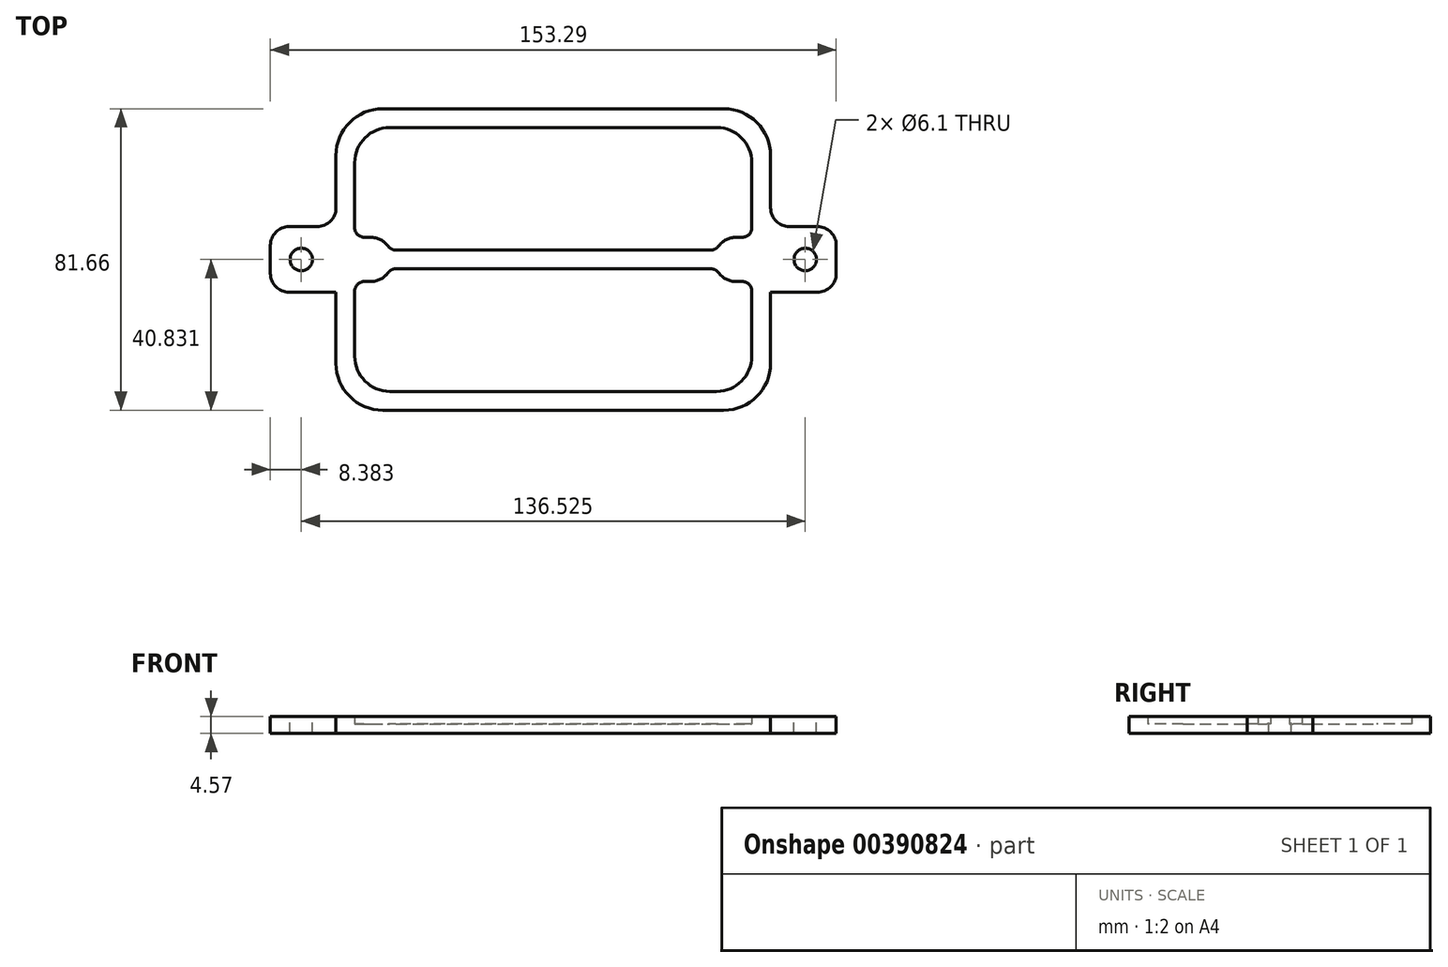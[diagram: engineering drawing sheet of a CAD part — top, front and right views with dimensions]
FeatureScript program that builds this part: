
annotation { "Feature Type Name" : "Feature", "Feature Type Description" : "" }
export const myFeature = defineFeature(function(context is Context, id is Id, definition is map)
    precondition{}
    {
        {
            var Q0;
            Q0=qCreatedBy(makeId("Top.planeOp"),FACE);
            var sketch = newSketch(context, id + "F0", { "sketchPlane" : qUnion([Q0])});
            skLineSegment(sketch, "E0.bottom", {"start": v(0, 0) * mm, "end": v(-117.73, 0) * mm});
            skLineSegment(sketch, "E0.top", {"start": v(0, 81.66) * mm, "end": v(-117.73, 81.66) * mm});
            skLineSegment(sketch, "E0.left", {"start": v(0, 0) * mm, "end": v(0, 81.66) * mm});
            skLineSegment(sketch, "E0.right", {"start": v(-117.73, 0) * mm, "end": v(-117.73, 81.66) * mm});
            skSolve(sketch);
        }
        {
            var Q0;
            Q0 = qSketchRegion(id + "F0", true);
            extrude(context, id + "F1", {"entities" : qUnion([Q0]), "depth" : 2.54 * mm});
        }
        {
            var Q0;
            Q0=makeQuery(id+"F1.opExtrude","CAP_FACE",FACE,{"disambiguationData":[OSD([sQuery(id+"F0.wireOp",EDGE,"E0.bottom"),sQuery(id+"F0.wireOp",EDGE,"E0.top"),sQuery(id+"F0.wireOp",EDGE,"E0.left"),sQuery(id+"F0.wireOp",EDGE,"E0.right")])],"isStart":false});
            var sketch = newSketch(context, id + "F2", { "sketchPlane" : qUnion([Q0])});
            skLineSegment(sketch, "E1.0", {"start": v(-14.6, 5.08) * mm, "end": v(-103.12, 5.08) * mm});
            skLineSegment(sketch, "E1.1", {"start": v(-5.08, 14.6) * mm, "end": v(-5.08, 32.3) * mm});
            skLineSegment(sketch, "E1.2", {"start": v(-14.6, 76.58) * mm, "end": v(-103.12, 76.58) * mm});
            skLineSegment(sketch, "E1.3", {"start": v(-112.65, 14.6) * mm, "end": v(-112.65, 32.3) * mm});
            skArc(sketch, "E2", {"start": v(-108.4, 34.83) * mm, "mid": v(-105.7, 35.47) * mm, "end": v(-103.57, 37.26) * mm});
            skLineSegment(sketch, "E3", {"start": v(-110.1, 34.83) * mm, "end": v(-108.4, 34.83) * mm});
            skLineSegment(sketch, "E4", {"start": v(-110.1, 46.83) * mm, "end": v(-108.4, 46.83) * mm});
            skLineSegment(sketch, "E5.trimOffspring", {"start": v(-112.65, 49.37) * mm, "end": v(-112.65, 67.06) * mm});
            skLineSegment(sketch, "E6", {"start": v(-58.86, 0) * mm, "end": v(-58.86, 38.3) * mm, "construction": true});
            skLineSegment(sketch, "E7.bottom", {"start": v(-101.53, 43.37) * mm, "end": v(-58.86, 43.37) * mm});
            skLineSegment(sketch, "E7.top", {"start": v(-101.53, 38.3) * mm, "end": v(-58.86, 38.3) * mm});
            skArc(sketch, "E8.trimOffspring", {"start": v(-103.57, 44.4) * mm, "mid": v(-105.7, 46.19) * mm, "end": v(-108.4, 46.83) * mm});
            skLineSegment(sketch, "E9.MirrorCS", {"start": v(-7.62, 46.83) * mm, "end": v(-9.33, 46.83) * mm});
            skArc(sketch, "E10.MirrorCS", {"start": v(-14.16, 44.4) * mm, "mid": v(-12.04, 46.19) * mm, "end": v(-9.33, 46.83) * mm});
            skLineSegment(sketch, "E11.MirrorCS", {"start": v(-16.2, 43.37) * mm, "end": v(-58.86, 43.37) * mm});
            skLineSegment(sketch, "E12.MirrorCS", {"start": v(-16.2, 38.3) * mm, "end": v(-58.86, 38.3) * mm});
            skArc(sketch, "E13.MirrorCS", {"start": v(-9.33, 34.83) * mm, "mid": v(-12.04, 35.47) * mm, "end": v(-14.16, 37.26) * mm});
            skLineSegment(sketch, "E14.MirrorCS", {"start": v(-7.62, 34.83) * mm, "end": v(-9.33, 34.83) * mm});
            skLineSegment(sketch, "E15.trimOffspring", {"start": v(-58.86, 43.37) * mm, "end": v(-58.86, 81.66) * mm, "construction": true});
            skLineSegment(sketch, "E16.trimOffspring", {"start": v(-5.08, 49.37) * mm, "end": v(-5.08, 67.06) * mm});
            skPoint(sketch, "E17.visualSharp", {"position": v(-112.65, 76.58) * mm});
            skArc(sketch, "E17.filletArc", {"start": v(-103.12, 76.58) * mm, "mid": v(-109.86, 73.8) * mm, "end": v(-112.65, 67.06) * mm});
            skPoint(sketch, "E18.visualSharp", {"position": v(-5.08, 76.58) * mm});
            skArc(sketch, "E18.filletArc", {"start": v(-5.08, 67.06) * mm, "mid": v(-7.87, 73.8) * mm, "end": v(-14.6, 76.58) * mm});
            skPoint(sketch, "E19.visualSharp", {"position": v(-5.08, 5.08) * mm});
            skArc(sketch, "E19.filletArc", {"start": v(-14.6, 5.08) * mm, "mid": v(-7.87, 7.87) * mm, "end": v(-5.08, 14.6) * mm});
            skPoint(sketch, "E20.visualSharp", {"position": v(-112.65, 5.08) * mm});
            skArc(sketch, "E20.filletArc", {"start": v(-112.65, 14.6) * mm, "mid": v(-109.86, 7.87) * mm, "end": v(-103.12, 5.08) * mm});
            skPoint(sketch, "E21.visualSharp", {"position": v(-112.65, 34.83) * mm});
            skArc(sketch, "E21.filletArc", {"start": v(-110.1, 34.83) * mm, "mid": v(-111.9, 34.09) * mm, "end": v(-112.65, 32.3) * mm});
            skPoint(sketch, "E22.visualSharp", {"position": v(-112.65, 46.83) * mm});
            skArc(sketch, "E22.filletArc", {"start": v(-112.65, 49.37) * mm, "mid": v(-111.9, 47.57) * mm, "end": v(-110.1, 46.83) * mm});
            skPoint(sketch, "E23.visualSharp", {"position": v(-102.96, 43.37) * mm});
            skArc(sketch, "E23.filletArc", {"start": v(-103.57, 44.4) * mm, "mid": v(-102.67, 43.64) * mm, "end": v(-101.53, 43.37) * mm});
            skPoint(sketch, "E24.visualSharp", {"position": v(-102.96, 38.3) * mm});
            skArc(sketch, "E24.filletArc", {"start": v(-101.53, 38.3) * mm, "mid": v(-102.67, 38.02) * mm, "end": v(-103.57, 37.26) * mm});
            skPoint(sketch, "E25.visualSharp", {"position": v(-5.08, 34.83) * mm});
            skArc(sketch, "E25.filletArc", {"start": v(-5.08, 32.3) * mm, "mid": v(-5.82, 34.09) * mm, "end": v(-7.62, 34.83) * mm});
            skPoint(sketch, "E26.visualSharp", {"position": v(-5.08, 46.83) * mm});
            skArc(sketch, "E26.filletArc", {"start": v(-7.62, 46.83) * mm, "mid": v(-5.82, 47.57) * mm, "end": v(-5.08, 49.37) * mm});
            skPoint(sketch, "E27.visualSharp", {"position": v(-14.77, 43.37) * mm});
            skArc(sketch, "E27.filletArc", {"start": v(-16.2, 43.37) * mm, "mid": v(-15.06, 43.64) * mm, "end": v(-14.16, 44.4) * mm});
            skPoint(sketch, "E28.visualSharp", {"position": v(-14.77, 38.3) * mm});
            skArc(sketch, "E28.filletArc", {"start": v(-14.16, 37.26) * mm, "mid": v(-15.06, 38.02) * mm, "end": v(-16.2, 38.3) * mm});
            skLineSegment(sketch, "E29.0", {"start": v(0, 81.66) * mm, "end": v(-117.73, 81.66) * mm});
            skLineSegment(sketch, "E30.0", {"start": v(-117.73, 0) * mm, "end": v(-117.73, 81.66) * mm});
            skLineSegment(sketch, "E31.0", {"start": v(0, 0) * mm, "end": v(-117.73, 0) * mm});
            skLineSegment(sketch, "E32.0", {"start": v(0, 0) * mm, "end": v(0, 81.66) * mm});
            skSolve(sketch);
        }
        {
            var Q0;
            Q0 = qSketchRegion(id + "F2", true);
            extrude(context, id + "F3", {"entities" : qUnion([Q0]), "operationType" : NewBodyOperationType.ADD, "depth" : 2.03 * mm});
        }
        {
            var Q0;
            Q0=makeQuery(id+"F3.boolean.opBoolean","MERGE",EDGE,{"derivedFrom":[makeQuery(id+"F1.opExtrude","SWEPT_EDGE",EDGE,{"disambiguationData":[OSD([sQuery(id+"F0.wireOp",EDGE,"E0.bottom"),sQuery(id+"F0.wireOp",EDGE,"E0.right")])]}),makeQuery(id+"F3.opExtrude","SWEPT_EDGE",EDGE,{"disambiguationData":[OSD([sQuery(id+"F2.wireOp",EDGE,"E30.0"),sQuery(id+"F2.wireOp",EDGE,"E31.0")])]})]});
            var Q1;
            Q1=makeQuery(id+"F3.boolean.opBoolean","MERGE",EDGE,{"derivedFrom":[makeQuery(id+"F1.opExtrude","SWEPT_EDGE",EDGE,{"disambiguationData":[OSD([sQuery(id+"F0.wireOp",EDGE,"E0.top"),sQuery(id+"F0.wireOp",EDGE,"E0.right")])]}),makeQuery(id+"F3.opExtrude","SWEPT_EDGE",EDGE,{"disambiguationData":[OSD([sQuery(id+"F2.wireOp",EDGE,"E29.0"),sQuery(id+"F2.wireOp",EDGE,"E30.0")])]})]});
            var Q2;
            Q2=makeQuery(id+"F3.boolean.opBoolean","MERGE",EDGE,{"derivedFrom":[makeQuery(id+"F1.opExtrude","SWEPT_EDGE",EDGE,{"disambiguationData":[OSD([sQuery(id+"F0.wireOp",EDGE,"E0.top"),sQuery(id+"F0.wireOp",EDGE,"E0.left")])]}),makeQuery(id+"F3.opExtrude","SWEPT_EDGE",EDGE,{"disambiguationData":[OSD([sQuery(id+"F2.wireOp",EDGE,"E29.0"),sQuery(id+"F2.wireOp",EDGE,"E32.0")])]})]});
            var Q3;
            Q3=makeQuery(id+"F3.boolean.opBoolean","MERGE",EDGE,{"derivedFrom":[makeQuery(id+"F1.opExtrude","SWEPT_EDGE",EDGE,{"disambiguationData":[OSD([sQuery(id+"F0.wireOp",EDGE,"E0.bottom"),sQuery(id+"F0.wireOp",EDGE,"E0.left")])]}),makeQuery(id+"F3.opExtrude","SWEPT_EDGE",EDGE,{"disambiguationData":[OSD([sQuery(id+"F2.wireOp",EDGE,"E31.0"),sQuery(id+"F2.wireOp",EDGE,"E32.0")])]})]});
            fillet(context, id + "F4", {"entities" : qUnion([Q0, Q1, Q2, Q3]), "radius" : 12.7 * mm, "tangentPropagation" : true, "allowEdgeOverflow" : false});
        }
        {
            var Q0;
            Q0=makeQuery(id+"F3.opExtrude","CAP_FACE",FACE,{"disambiguationData":[OSD([sQuery(id+"F2.wireOp",EDGE,"E1.0"),sQuery(id+"F2.wireOp",EDGE,"E1.1"),sQuery(id+"F2.wireOp",EDGE,"E1.2"),sQuery(id+"F2.wireOp",EDGE,"E1.3"),sQuery(id+"F2.wireOp",EDGE,"E2"),sQuery(id+"F2.wireOp",EDGE,"E3"),sQuery(id+"F2.wireOp",EDGE,"E4"),sQuery(id+"F2.wireOp",EDGE,"E5.trimOffspring"),sQuery(id+"F2.wireOp",EDGE,"E7.bottom"),sQuery(id+"F2.wireOp",EDGE,"E7.top"),sQuery(id+"F2.wireOp",EDGE,"E8.trimOffspring"),sQuery(id+"F2.wireOp",EDGE,"E9.MirrorCS"),sQuery(id+"F2.wireOp",EDGE,"E10.MirrorCS"),sQuery(id+"F2.wireOp",EDGE,"E11.MirrorCS"),sQuery(id+"F2.wireOp",EDGE,"E12.MirrorCS"),sQuery(id+"F2.wireOp",EDGE,"E13.MirrorCS"),sQuery(id+"F2.wireOp",EDGE,"E14.MirrorCS"),sQuery(id+"F2.wireOp",EDGE,"E16.trimOffspring"),sQuery(id+"F2.wireOp",EDGE,"E17.filletArc"),sQuery(id+"F2.wireOp",EDGE,"E18.filletArc"),sQuery(id+"F2.wireOp",EDGE,"E19.filletArc"),sQuery(id+"F2.wireOp",EDGE,"E20.filletArc"),sQuery(id+"F2.wireOp",EDGE,"E21.filletArc"),sQuery(id+"F2.wireOp",EDGE,"E22.filletArc"),sQuery(id+"F2.wireOp",EDGE,"E23.filletArc"),sQuery(id+"F2.wireOp",EDGE,"E24.filletArc"),sQuery(id+"F2.wireOp",EDGE,"E25.filletArc"),sQuery(id+"F2.wireOp",EDGE,"E26.filletArc"),sQuery(id+"F2.wireOp",EDGE,"E27.filletArc"),sQuery(id+"F2.wireOp",EDGE,"E28.filletArc"),sQuery(id+"F2.wireOp",EDGE,"E29.0"),sQuery(id+"F2.wireOp",EDGE,"E30.0"),sQuery(id+"F2.wireOp",EDGE,"E31.0"),sQuery(id+"F2.wireOp",EDGE,"E32.0")])],"isStart":false});
            var sketch = newSketch(context, id + "F5", { "sketchPlane" : qUnion([Q0])});
            skLineSegment(sketch, "E33.bottom", {"start": v(0, 31.94) * mm, "end": v(17.78, 31.94) * mm});
            skLineSegment(sketch, "E33.top", {"start": v(0, 49.72) * mm, "end": v(17.78, 49.72) * mm});
            skLineSegment(sketch, "E33.left", {"start": v(0, 31.94) * mm, "end": v(0, 49.72) * mm});
            skLineSegment(sketch, "E33.right", {"start": v(17.78, 31.94) * mm, "end": v(17.78, 49.72) * mm});
            skLineSegment(sketch, "E34", {"start": v(-117.73, 40.83) * mm, "end": v(0, 40.83) * mm, "construction": true});
            skSolve(sketch);
        }
        {
            var Q0;
            Q0 = qSketchRegion(id + "F5", true);
            var Q1;
            Q1=makeQuery(id+"F1.opExtrude","CAP_FACE",FACE,{"disambiguationData":[OSD([sQuery(id+"F0.wireOp",EDGE,"E0.bottom"),sQuery(id+"F0.wireOp",EDGE,"E0.top"),sQuery(id+"F0.wireOp",EDGE,"E0.left"),sQuery(id+"F0.wireOp",EDGE,"E0.right")])],"isStart":true});
            extrude(context, id + "F6", {"entities" : qUnion([Q0]), "operationType" : NewBodyOperationType.ADD, "endBound" : BoundingType.UP_TO_SURFACE, "oppositeDirection" : true, "endBoundEntityFace" : qUnion([Q1]), "depth" : 25.4 * mm});
        }
        {
            var Q0;
            Q0=makeQuery(id+"F6.opExtrude","SWEPT_EDGE",EDGE,{"disambiguationData":[OSD([sQuery(id+"F2.wireOp",EDGE,"E32.0"),sQuery(id+"F5.wireOp",EDGE,"E33.bottom"),sQuery(id+"F5.wireOp",EDGE,"E33.left")])]});
            var Q1;
            Q1=makeQuery(id+"F6.opExtrude","SWEPT_EDGE",EDGE,{"disambiguationData":[OSD([sQuery(id+"F2.wireOp",EDGE,"E32.0"),sQuery(id+"F5.wireOp",EDGE,"E33.top"),sQuery(id+"F5.wireOp",EDGE,"E33.left")])]});
            var Q2;
            Q2=makeQuery(id+"F6.opExtrude","SWEPT_EDGE",EDGE,{"disambiguationData":[OSD([sQuery(id+"F5.wireOp",EDGE,"E33.top"),sQuery(id+"F5.wireOp",EDGE,"E33.right")])]});
            var Q3;
            Q3=makeQuery(id+"F6.opExtrude","SWEPT_EDGE",EDGE,{"disambiguationData":[OSD([sQuery(id+"F5.wireOp",EDGE,"E33.bottom"),sQuery(id+"F5.wireOp",EDGE,"E33.right")])]});
            fillet(context, id + "F7", {"entities" : qUnion([Q0, Q1, Q2, Q3]), "radius" : 5.08 * mm, "tangentPropagation" : true, "allowEdgeOverflow" : false});
        }
        {
            var Q0;
            Q0=makeQuery(id+"F3.opExtrude","CAP_EDGE",EDGE,{"disambiguationData":[OSD([sQuery(id+"F2.wireOp",EDGE,"E29.0")])],"isStart":false});
            cPoint(context, id + "F8", {"entities" : qUnion([Q0]), "parameter" : 0.5});
        }
        {
            var Q0;
            Q0=makeQuery(id+"F3.opExtrude","CAP_EDGE",EDGE,{"disambiguationData":[OSD([sQuery(id+"F2.wireOp",EDGE,"E7.bottom"),sQuery(id+"F2.wireOp",EDGE,"E11.MirrorCS")])],"isStart":false});
            cPoint(context, id + "F9", {"entities" : qUnion([Q0]), "parameter" : 0.5});
        }
        {
            var Q0;
            Q0=makeQuery(id+"F3.opExtrude","CAP_EDGE",EDGE,{"disambiguationData":[OSD([sQuery(id+"F2.wireOp",EDGE,"E1.0")])],"isStart":true});
            cPoint(context, id + "F10", {"entities" : qUnion([Q0]), "parameter" : 0.5});
        }
        {
            var Q0;
            Q0 = qCreatedBy(id + "F8" ,VERTEX);
            var Q1;
            Q1 = qCreatedBy(id + "F9" ,VERTEX);
            var Q2;
            Q2 = qCreatedBy(id + "F10" ,VERTEX);
            cPlane(context, id + "F11", {"entities" : qUnion([Q0, Q1, Q2]), "cplaneType" : CPlaneType.THREE_POINT, "offset" : 25.4 * mm, "width" : 152.4 * mm, "height" : 152.4 * mm});
        }
        {
            var Q0;
            Q0=makeQuery(id+"F1.opExtrude","SWEPT_BODY",BODY,{"disambiguationData":[OSD([sQuery(id+"F0.wireOp",EDGE,"E0.bottom"),sQuery(id+"F0.wireOp",EDGE,"E0.top"),sQuery(id+"F0.wireOp",EDGE,"E0.left"),sQuery(id+"F0.wireOp",EDGE,"E0.right")])]});
            var Q1;
            Q1=qCreatedBy(id+"F11.planeOp",FACE);
            mirror(context, id + "F12", {"operationType" : NewBodyOperationType.ADD, "entities" : qUnion([Q0]), "mirrorPlane" : qUnion([Q1])});
        }
        {
            var Q0;
            {var subQ0=makeQuery(id+"F6.boolean.opBoolean","MERGE",FACE,{"derivedFrom":[makeQuery(id+"F3.opExtrude","CAP_FACE",FACE,{"disambiguationData":[OSD([sQuery(id+"F2.wireOp",EDGE,"E1.0"),sQuery(id+"F2.wireOp",EDGE,"E1.1"),sQuery(id+"F2.wireOp",EDGE,"E1.2"),sQuery(id+"F2.wireOp",EDGE,"E1.3"),sQuery(id+"F2.wireOp",EDGE,"E2"),sQuery(id+"F2.wireOp",EDGE,"E3"),sQuery(id+"F2.wireOp",EDGE,"E4"),sQuery(id+"F2.wireOp",EDGE,"E5.trimOffspring"),sQuery(id+"F2.wireOp",EDGE,"E7.bottom"),sQuery(id+"F2.wireOp",EDGE,"E7.top"),sQuery(id+"F2.wireOp",EDGE,"E8.trimOffspring"),sQuery(id+"F2.wireOp",EDGE,"E9.MirrorCS"),sQuery(id+"F2.wireOp",EDGE,"E10.MirrorCS"),sQuery(id+"F2.wireOp",EDGE,"E11.MirrorCS"),sQuery(id+"F2.wireOp",EDGE,"E12.MirrorCS"),sQuery(id+"F2.wireOp",EDGE,"E13.MirrorCS"),sQuery(id+"F2.wireOp",EDGE,"E14.MirrorCS"),sQuery(id+"F2.wireOp",EDGE,"E16.trimOffspring"),sQuery(id+"F2.wireOp",EDGE,"E17.filletArc"),sQuery(id+"F2.wireOp",EDGE,"E18.filletArc"),sQuery(id+"F2.wireOp",EDGE,"E19.filletArc"),sQuery(id+"F2.wireOp",EDGE,"E20.filletArc"),sQuery(id+"F2.wireOp",EDGE,"E21.filletArc"),sQuery(id+"F2.wireOp",EDGE,"E22.filletArc"),sQuery(id+"F2.wireOp",EDGE,"E23.filletArc"),sQuery(id+"F2.wireOp",EDGE,"E24.filletArc"),sQuery(id+"F2.wireOp",EDGE,"E25.filletArc"),sQuery(id+"F2.wireOp",EDGE,"E26.filletArc"),sQuery(id+"F2.wireOp",EDGE,"E27.filletArc"),sQuery(id+"F2.wireOp",EDGE,"E28.filletArc"),sQuery(id+"F2.wireOp",EDGE,"E29.0"),sQuery(id+"F2.wireOp",EDGE,"E30.0"),sQuery(id+"F2.wireOp",EDGE,"E31.0"),sQuery(id+"F2.wireOp",EDGE,"E32.0")])],"isStart":false}),makeQuery(id+"F6.opExtrude","CAP_FACE",FACE,{"disambiguationData":[OSD([sQuery(id+"F5.wireOp",EDGE,"E33.bottom"),sQuery(id+"F5.wireOp",EDGE,"E33.top"),sQuery(id+"F5.wireOp",EDGE,"E33.left"),sQuery(id+"F5.wireOp",EDGE,"E33.right")])],"isStart":true})]});Q0=makeQuery(id+"F12.boolean.opBoolean","MERGE",FACE,{"derivedFrom":[subQ0,makeQuery(id+"F12.opPattern","COPY",FACE,{"derivedFrom":subQ0,"instanceName":"1"})]});}
            var sketch = newSketch(context, id + "F13", { "sketchPlane" : qUnion([Q0])});
            skCircle(sketch, "E35", {"center": v(9.4, 40.83) * mm, "radius": 3.05 * mm});
            skLineSegment(sketch, "E36", {"start": v(-9.33, 40.83) * mm, "end": v(-123.45, 40.83) * mm, "construction": true});
            skCircle(sketch, "E37.MirrorC", {"center": v(-127.13, 40.83) * mm, "radius": 3.05 * mm});
            skSolve(sketch);
        }
        {
            var Q0;
            Q0 = qSketchRegion(id + "F13", true);
            extrude(context, id + "F14", {"entities" : qUnion([Q0]), "operationType" : NewBodyOperationType.REMOVE, "endBound" : BoundingType.THROUGH_ALL, "oppositeDirection" : true, "depth" : 25.4 * mm});
        }
    });
